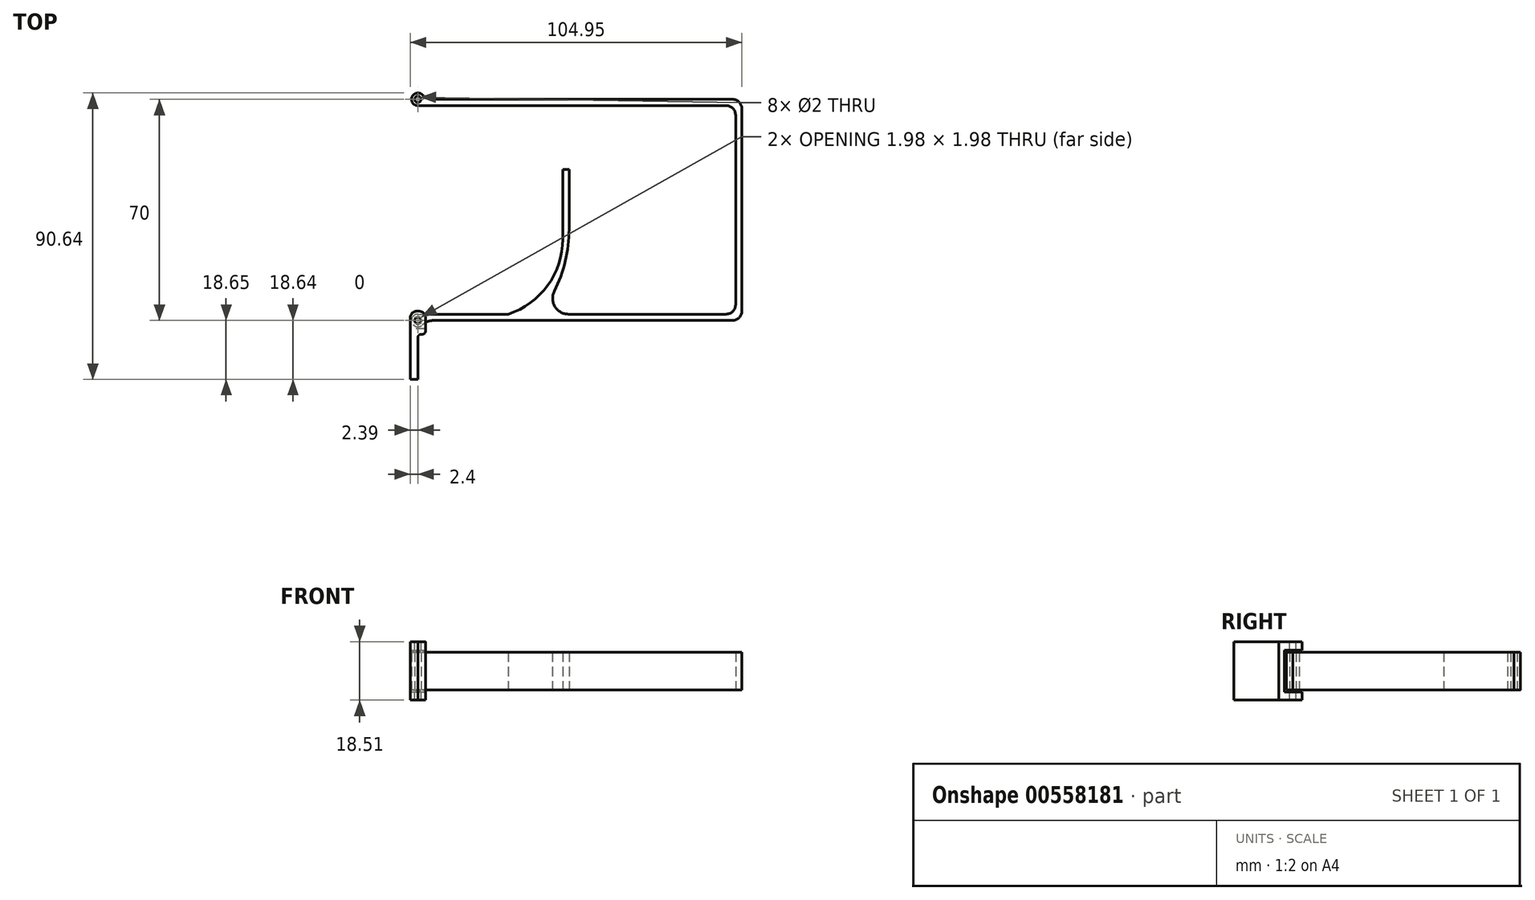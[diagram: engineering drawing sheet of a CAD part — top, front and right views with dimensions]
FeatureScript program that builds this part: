
annotation { "Feature Type Name" : "Feature", "Feature Type Description" : "" }
export const myFeature = defineFeature(function(context is Context, id is Id, definition is map)
    precondition{}
    {
        {
            var Q0;
            Q0=qCreatedBy(makeId("Top.planeOp"),FACE);
            var sketch = newSketch(context, id + "F0", { "sketchPlane" : qUnion([Q0])});
            skLineSegment(sketch, "E0.top", {"start": v(0, 2) * mm, "end": v(28.55, 2) * mm});
            skArc(sketch, "E1", {"start": v(0, 2) * mm, "mid": v(-1.85, -0.76) * mm, "end": v(1.4, -1.43) * mm});
            skCircle(sketch, "E2", {"center": v(0, 0) * mm, "radius": 1 * mm});
            skLineSegment(sketch, "E3.trimOffspring", {"start": v(4.9, 0) * mm, "end": v(99.55, 0) * mm});
            skPoint(sketch, "E4.visualSharp", {"position": v(2, 0) * mm});
            skArc(sketch, "E4.filletArc", {"start": v(4.9, 0) * mm, "mid": v(3, -0.37) * mm, "end": v(1.4, -1.43) * mm});
            skPoint(sketch, "E5.center.orphan", {"position": v(48.42, 4) * mm});
            skLineSegment(sketch, "E6.top", {"start": v(45.85, 47.76) * mm, "end": v(47.85, 47.76) * mm});
            skLineSegment(sketch, "E6.left", {"start": v(45.85, 25.76) * mm, "end": v(45.85, 47.76) * mm});
            skLineSegment(sketch, "E6.right", {"start": v(47.85, 28.88) * mm, "end": v(47.85, 47.76) * mm});
            skArc(sketch, "E7", {"start": v(45.85, 25.76) * mm, "mid": v(41.07, 11.06) * mm, "end": v(28.55, 2) * mm});
            skArc(sketch, "E8", {"start": v(47.85, 28.88) * mm, "mid": v(46.67, 18.8) * mm, "end": v(43.18, 9.26) * mm});
            skLineSegment(sketch, "E9.trimOffspring", {"start": v(47.64, 2) * mm, "end": v(97.55, 2) * mm});
            skLineSegment(sketch, "E10.left", {"start": v(102.55, 3) * mm, "end": v(102.55, 67) * mm});
            skLineSegment(sketch, "E10.right", {"start": v(100.55, 5) * mm, "end": v(100.55, 65) * mm});
            skPoint(sketch, "E11.visualSharp", {"position": v(38.55, 2) * mm});
            skArc(sketch, "E11.filletArc", {"start": v(43.18, 9.26) * mm, "mid": v(43.38, 4.38) * mm, "end": v(47.64, 2) * mm});
            skPoint(sketch, "E12.visualSharp", {"position": v(100.55, 2) * mm});
            skArc(sketch, "E12.filletArc", {"start": v(97.55, 2) * mm, "mid": v(99.67, 2.88) * mm, "end": v(100.55, 5) * mm});
            skPoint(sketch, "E13.visualSharp", {"position": v(102.55, 0) * mm});
            skArc(sketch, "E13.filletArc", {"start": v(99.55, 0) * mm, "mid": v(101.67, 0.88) * mm, "end": v(102.55, 3) * mm});
            skLineSegment(sketch, "E14.bottom", {"start": v(99.55, 70) * mm, "end": v(4.9, 70) * mm});
            skLineSegment(sketch, "E14.top", {"start": v(97.55, 68) * mm, "end": v(0, 68) * mm});
            skPoint(sketch, "E15.visualSharp", {"position": v(100.55, 68) * mm});
            skArc(sketch, "E15.filletArc", {"start": v(100.55, 65) * mm, "mid": v(99.67, 67.12) * mm, "end": v(97.55, 68) * mm});
            skPoint(sketch, "E16.visualSharp", {"position": v(102.55, 70) * mm});
            skArc(sketch, "E16.filletArc", {"start": v(102.55, 67) * mm, "mid": v(101.67, 69.12) * mm, "end": v(99.55, 70) * mm});
            skArc(sketch, "E17", {"start": v(1.4, 71.43) * mm, "mid": v(-1.85, 70.76) * mm, "end": v(0, 68) * mm});
            skCircle(sketch, "E18", {"center": v(0, 70) * mm, "radius": 1 * mm});
            skPoint(sketch, "E19.visualSharp", {"position": v(2, 70) * mm});
            skArc(sketch, "E19.filletArc", {"start": v(1.4, 71.43) * mm, "mid": v(3, 70.37) * mm, "end": v(4.9, 70) * mm});
            skSolve(sketch);
        }
        {
            var Q0;
            Q0=makeQuery(id+"F0.imprint","IMPRINT",FACE,{"disambiguationData":[TD([[makeQuery(id+"F0.imprint","IMPRINT",EDGE,{"derivedFrom":sQuery(id+"F0.wireOp",EDGE,"E0.top")}),-1.0]])]});
            extrude(context, id + "F1", {"entities" : qUnion([Q0]), "depth" : 12 * mm, "offsetDistance" : 25 * mm});
        }
        {
            var Q0;
            Q0=qCreatedBy(makeId("Right.planeOp"),FACE);
            var sketch = newSketch(context, id + "F2", { "sketchPlane" : qUnion([Q0])});
            skLineSegment(sketch, "E20.bottom", {"start": v(2.92, -3.17) * mm, "end": v(-18.64, -3.17) * mm});
            skLineSegment(sketch, "E20.top", {"start": v(2.92, 15.34) * mm, "end": v(-18.64, 15.34) * mm});
            skLineSegment(sketch, "E20.left", {"start": v(2.92, -3.17) * mm, "end": v(2.92, -0.59) * mm});
            skLineSegment(sketch, "E20.right", {"start": v(-18.64, -3.17) * mm, "end": v(-18.64, 15.34) * mm});
            skLineSegment(sketch, "E21.bottom", {"start": v(2.92, 12.62) * mm, "end": v(-2.6, 12.62) * mm});
            skLineSegment(sketch, "E21.top", {"start": v(2.92, -0.59) * mm, "end": v(-2.6, -0.59) * mm});
            skLineSegment(sketch, "E21.right", {"start": v(-2.6, 12.62) * mm, "end": v(-2.6, -0.59) * mm});
            skLineSegment(sketch, "E22.trimOffspring", {"start": v(2.92, 12.62) * mm, "end": v(2.92, 15.34) * mm});
            skSolve(sketch);
        }
        {
            var Q0;
            Q0 = qSketchRegion(id + "F2", true);
            extrude(context, id + "F3", {"entities" : qUnion([Q0]), "endBound" : BoundingType.SYMMETRIC, "depth" : 4.8 * mm, "offsetDistance" : 25 * mm});
        }
        {
            var Q0;
            Q0=makeQuery(id+"F3.opExtrude","SWEPT_FACE",FACE,{"disambiguationData":[OSD([sQuery(id+"F2.wireOp",EDGE,"E20.top")])]});
            var sketch = newSketch(context, id + "F4", { "sketchPlane" : qUnion([Q0])});
            skCircle(sketch, "E23", {"center": v(0, 0) * mm, "radius": 1 * mm});
            skSolve(sketch);
        }
        {
            var Q0;
            Q0 = qSketchRegion(id + "F4", true);
            extrude(context, id + "F5", {"entities" : qUnion([Q0]), "operationType" : NewBodyOperationType.REMOVE, "oppositeDirection" : true, "depth" : 25 * mm, "offsetDistance" : 25 * mm});
        }
        {
            var Q0;
            Q0=makeQuery(id+"F3.opExtrude","CAP_EDGE",EDGE,{"disambiguationData":[OSD([sQuery(id+"F2.wireOp",EDGE,"E20.left")])],"isStart":true});
            var Q1;
            Q1=makeQuery(id+"F3.opExtrude","CAP_EDGE",EDGE,{"disambiguationData":[OSD([sQuery(id+"F2.wireOp",EDGE,"E20.left")])],"isStart":false});
            var Q2;
            Q2=makeQuery(id+"F3.opExtrude","CAP_EDGE",EDGE,{"disambiguationData":[OSD([sQuery(id+"F2.wireOp",EDGE,"E22.trimOffspring")])],"isStart":true});
            var Q3;
            Q3=makeQuery(id+"F3.opExtrude","CAP_EDGE",EDGE,{"disambiguationData":[OSD([sQuery(id+"F2.wireOp",EDGE,"E22.trimOffspring")])],"isStart":false});
            fillet(context, id + "F6", {"entities" : qUnion([Q0, Q1, Q2, Q3]), "radius" : 2 * mm, "tangentPropagation" : true, "allowEdgeOverflow" : false});
        }
        {
            var Q0;
            Q0=makeQuery(id+"F3.opExtrude","SWEPT_FACE",FACE,{"disambiguationData":[OSD([sQuery(id+"F2.wireOp",EDGE,"E20.top")])]});
            var sketch = newSketch(context, id + "F7", { "sketchPlane" : qUnion([Q0])});
            skLineSegment(sketch, "E24.bottom", {"start": v(0, -4.38) * mm, "end": v(2.98, -4.38) * mm});
            skLineSegment(sketch, "E24.top", {"start": v(0, -19.26) * mm, "end": v(2.98, -19.26) * mm});
            skLineSegment(sketch, "E24.left", {"start": v(0, -4.38) * mm, "end": v(0, -19.26) * mm});
            skLineSegment(sketch, "E24.right", {"start": v(2.98, -4.38) * mm, "end": v(2.98, -19.26) * mm});
            skSolve(sketch);
        }
        {
            var Q0;
            Q0 = qSketchRegion(id + "F7", true);
            extrude(context, id + "F8", {"entities" : qUnion([Q0]), "operationType" : NewBodyOperationType.REMOVE, "oppositeDirection" : true, "depth" : 25 * mm, "offsetDistance" : 25 * mm});
        }
        {
            var Q0;
            Q0=makeQuery(id+"F8.boolean.opBoolean","INTERSECT",EDGE,{"derivedFrom":[makeQuery(id+"F3.opExtrude","CAP_FACE",FACE,{"disambiguationData":[OSD([sQuery(id+"F2.wireOp",EDGE,"E20.bottom"),sQuery(id+"F2.wireOp",EDGE,"E20.top"),sQuery(id+"F2.wireOp",EDGE,"E20.left"),sQuery(id+"F2.wireOp",EDGE,"E20.right"),sQuery(id+"F2.wireOp",EDGE,"E21.bottom"),sQuery(id+"F2.wireOp",EDGE,"E21.top"),sQuery(id+"F2.wireOp",EDGE,"E21.right"),sQuery(id+"F2.wireOp",EDGE,"E22.trimOffspring")])],"isStart":false}),makeQuery(id+"F8.opExtrude","SWEPT_FACE",FACE,{"disambiguationData":[OSD([sQuery(id+"F7.wireOp",EDGE,"E24.bottom")])]})]});
            var Q1;
            Q1=makeQuery(id+"F8.boolean.opBoolean","COPY",EDGE,{"derivedFrom":makeQuery(id+"F8.opExtrude","SWEPT_EDGE",EDGE,{"disambiguationData":[OSD([sQuery(id+"F7.wireOp",EDGE,"E24.bottom"),sQuery(id+"F7.wireOp",EDGE,"E24.left")])]})});
            fillet(context, id + "F9", {"entities" : qUnion([Q0, Q1]), "radius" : 1 * mm, "tangentPropagation" : true, "allowEdgeOverflow" : false});
        }
    });
